# Revit family: Table-Teknion-NFTS_Wood_Table_Square-R2020
name_source: partatom
category: Furniture
units: mm (PartAtom-declared; Revit-internal decimal feet)

## family parameters
Always vertical = Yes
Cut with Voids When Loaded = No
OmniClass Number = 23.40.20.00
OmniClass Title = General Furniture and Specialties
Room Calculation Point = No
Shared = Yes
Work Plane-Based = No

## types (3) — shared parameters
Assembly Code = E2020200
Manufacturer = Teknion
Manufacturer Fax = 416.661.4586
Part Number = NFTR
Product Line = North 56
Product Page URL = https://www.teknion.com
Series = North 56
Sustainability Data = https://www.teknion.com
URL = www.teknion.com
Unit Weight URL = http://www.teknion.com
Warranty = http://www.teknion.com
zero-valued in all types: Default Elevation

## per-type parameters (varying)
| type | Description | Diagonal dis | Height | Leg Dis | Leg Support | Leg Support Height | Model | Top Finish | Wood Leg Finish |
| 29" Height | Wood Table-Round, 29" Height,46" Size | 19.144 " | 29 " | 27.073 " | No | 6.113 " | NFTR2946 | Laminate - Teknion - LW - Storm White | Veneer - Teknion - MP - Natural Maple |
| 36" Height | Wood Table-Round, 36" Height,46" Size | 19.517 " | 36 " | 27.601 " | Yes | 6.113 " | NFTR3646 | <By Category> | <By Category> |
| 42" Height | Wood Table-Round, 42" Height,46" Size | 21.35 " | 42 " | 30.194 " | Yes | 12.113 " | NFTR4246 | Laminate - Teknion - 2T -Crisp Grey | Laminate - Teknion - LW - Storm White |

## geometry (parser evidence)
native form markers: Sweep x2
no freeform markers — native parametric forms only
